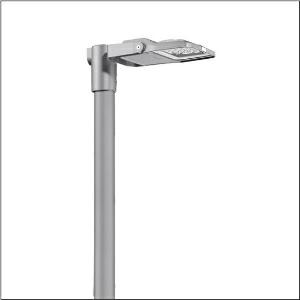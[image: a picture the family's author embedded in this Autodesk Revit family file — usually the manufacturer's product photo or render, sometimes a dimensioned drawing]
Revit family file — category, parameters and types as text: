
# Revit family: floodlight_fl_21_iq_micro___pl61_5xa7761a4c3a_000e
name_source: partatom
category: Lighting Fixtures
units: mm (PartAtom-declared; Revit-internal decimal feet)

## family parameters
Cut with Voids When Loaded = No
Host = Face
Light Source = No
Part Type = Normal
Room Calculation Point = No
Round Connector Dimension = Use Diameter
Shared = No

## types (1)
- --- (1 x LED, 3030 lm, 23.1 W, 4000K)
    Apparent Load = 23 VA
    CIE Flux Codes = 33 65 98 100 100
    Color Rendering = 70
    Color Temperature = 4000K
    Default Elevation = 1800 mm
    Description = Floodlight FL 21 iQ micro, floodlight, primary light control with lens, of PMMA, primary optical cover: protective disc, of toughened safety glass, transparent, light distribution: PL61, light emission: direct distribution, installation type: surface-mounted, lamps: LED, High Power LED, rated values: 3.030lm | 23,1W | 131,2lm/W (begin service life); end service life: 3.030lm | 23,8W; at 50% lumin. flux: 1.515lm | 11W | 137,7lm/W, colour temperature: 4000K, colour rendering: CRI > 70, light colour: 740, light setting 1 begin service life: 100% | 3.030lm | 23,1W | 131,2lm/W | 4.000K, light setting 1 end service life: 23,8W, further light settings possible, control: optimised constant luminous flux control (CLO 2.0), Desk-Remote (wireless, voltage-free reading and setting of iQ features in the workshop via application-optimized NFC function/RFID function), Light-Fading, Smart-Wire, Night-Set, Lumen-Switch, Temp-Guard, Auto-Match, pre-setting: linear dimming characteristic, with terminal, 6-pole, mains connection: 220..240V, AC, 50/60Hz, luminaire housing, of diecast aluminium, powder-coated, SITECO metallic grey (DB 702S), corrosivity category C5 mid according to DIN EN ISO 12944suitable for swimming poolschlorine-resistant, sealing non-destructively replaceable, please order mast flange separately, mast bracket, of steel, galvanised, powder-coated, SITECO metallic grey (DB 702S), protection rating (complete): IP66, insulation class (complete): insulation class II (safety insulation), certification: CE, ENEC, VDE, protection symbol: D, impact resistance: IK07, permissible operating ambient temperature: -40..+40°C, permissible operating ambient temperature for outdoor applications: -40..+50°C, standard: DIN EN 12944, LABS conformity tested according to VDMA 24364:2018-05, packaging unit: 1 piece

Light Distribution: PL61
    Height = 65 mm
    Lamp = 1 x LED
    Lamp Light Flux = 3030 lm
    Lamp Power = 23.1 W
    Lamp count = 1
    Length = 312 mm
    Luminous efficacy = 131 lm/W
    Manufacturer = Siteco
    ModVariant = No
    Model = 5XA7761A4C3A
    Mounting Place = Pole
    Mounting Type = Pole annexe
    Number of Poles = 1
    OnlyDefault = Yes
    Power Factor = 1
    Product Name = Floodlight FL 21 iQ micro | PL61
    Product group = floodlight | pylon annexe
    ProductGroupID = 6201
    Protection Class = Protection class II
    Protection Degree = IP 66
    RLX_Detail_Level = 1
    RLX_Emergency_Light_Flux = 0 lm
    RLX_Emergency_Type = 0
    RLX_Emergency_Type_DB = No
    RlxData = <blob elided: 102117 chars, md5=39833d83>
    Socket = socket
    Standby Power = 0 W
    System Light Flux = 3030 lm
    System Power = 23 W
    Type Comments = factory setting: luminous flux: 100 % | dim-lin: 254 | 455 mA
    Type Image = l_1007121.jpg
    URL = http://relux.com
    VarID = @adj_193533
    Voltage = 0 V
    Weight = 0.00 kg
    Width = 230 mm

## geometry (parser evidence)
native form markers: Blend x4, Sweep x13
no freeform markers — native parametric forms only
